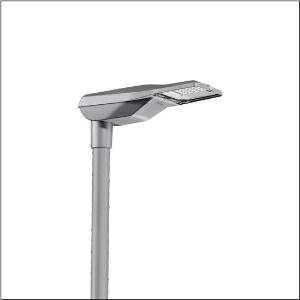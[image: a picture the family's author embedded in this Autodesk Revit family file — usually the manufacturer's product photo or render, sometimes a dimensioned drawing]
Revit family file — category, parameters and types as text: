
# Revit family: streetlight_sl_21_iq_micro___st0_8a_5xe1c61d08cb_7ac8
name_source: partatom
category: Lighting Fixtures
units: mm (PartAtom-declared; Revit-internal decimal feet)

## family parameters
Cut with Voids When Loaded = No
Host = Face
Light Source = No
Part Type = Normal
Room Calculation Point = No
Round Connector Dimension = Use Diameter
Shared = No

## types (1)
- --- (1 x LED, 2570 lm, 19.4 W, 2700K)
    Apparent Load = 19 VA
    CIE Flux Codes = 38 75 97 100 100
    Color Rendering = 70
    Color Temperature = 2700K
    Default Elevation = 1800 mm
    Description = Streetlight SL 21 iQ micro, mast luminaire, primary light control with lens, of PMMA, primary optical cover: cover, of toughened safety glass, transparent, light distribution: ST0.8a, light emission: direct distribution, primary light characteristic: asymmetric, installation type: post-top, side-entry, LED, High Power LED, rated luminous flux: 2.570lm, luminous efficacy: 133lm/W, light colour: 727, colour temperature: 2700K, control: Auto-Match, Temp-Guard, Lumen-Switch, Night-Set, Smart-Wire, Light-Fading, Desk-Remote (wireless, voltage-free reading and setting of iQ features in the workshop via application-optimized NFC function/RFID function), optimised constant luminous flux control (CLO 2.0), pre-setting: linear dimming characteristic, mains connection: 220..240V, AC, 50/60Hz, start of lifetime: 19W, end of service life: 20W, reduction: 10W, luminaire housing, of diecast aluminium, powder-coated, Siteco® metallic grey (DB 702S), corrosivity category C5 mid according to DIN EN ISO 12944, please order mast flange separately, inclination adjustable: 0°, 5°, 10°, 15°, sealing non-destructively replaceable, multi-level sealing system, length: 528mm, width: 235mm, height: 110mm, mast flange for spigot size: 42mm (side-entry): 5XC10008XM4, 60/48mm (side-entry/post-top): 5XC10108XM2, 76/60mm (side-entry/post-top): 5XC10108XM1, protection rating (complete): IP66, insulation class (complete): insulation class II (safety insulation), certification: CE, ENEC, ENEC+, VDE, impact resistance: IK09, permissible operating ambient temperature for outdoor applications: -40..+50°C, standard-compliant lighting for roads and squares, packaging unit: 1 piece

Light Distribution: ST0.8a
    Height = 110 mm
    Lamp = 1 x LED
    Lamp Light Flux = 2570 lm
    Lamp Power = 19.4 W
    Lamp count = 1
    Length = 528 mm
    Luminous efficacy = 132 lm/W
    Manufacturer = Siteco
    ModVariant = No
    Model = 5XE1C61D08CB
    Number of Poles = 1
    OnlyDefault = Yes
    Power Factor = 1
    Product Name = Streetlight SL 21 iQ micro | ST0.8a
    Product group = mast luminaire | pylon top
    ProductGroupID = 6100
    Protection Class = Protection class II
    Protection Degree = IP 66
    RLX_Detail_Level = 1
    RLX_Emergency_Light_Flux = 0 lm
    RLX_Emergency_Type = 0
    RLX_Emergency_Type_DB = No
    RlxData = <blob elided: 99477 chars, md5=ee2a180b>
    Socket = socket
    Standby Power = 0 W
    System Light Flux = 2570 lm
    System Power = 19 W
    Type Comments = factory setting: luminous flux: 100 % | dim-lin: 254 | 387 mA
    Type Image = l_1006881.jpg
    URL = http://relux.com
    VarID = @adj_108123
    Voltage = 0 V
    Weight = 0.00 kg
    Width = 235 mm

## geometry (parser evidence)
native form markers: Blend x4, Sweep x11
no freeform markers — native parametric forms only
